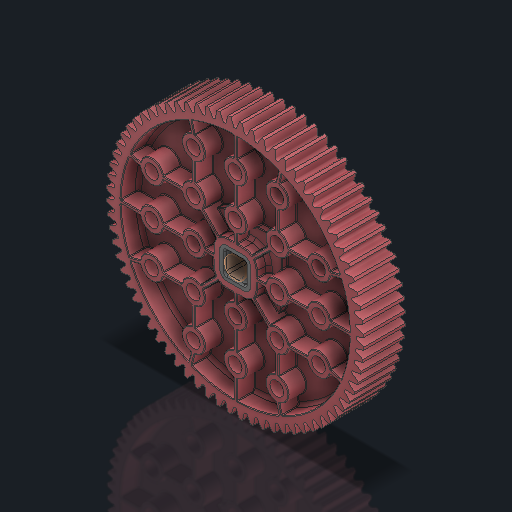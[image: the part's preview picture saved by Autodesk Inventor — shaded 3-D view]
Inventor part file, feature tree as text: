
AUTODESK INVENTOR PART (.ipt)
format: ipt  version: 2023.2 (Build 272271030, 271C)  size: 6,645,248 bytes
history: native  units: in
note: dims shown in document units (in); Inventor stores cm internally (conversion verified against a paired STEP export)
features: other x6, sketch x1
ambient origin geometry x8: Origin, YZ Plane, XZ Plane, XY Plane, X Axis, Y Axis, Z Axis, Center Point
bodies: Solid1 (feature_tree), Solid2 (feature_tree)
feature tree (7):
  other  "HS 72T Gear, No Insert.ipt"
  other  "Solid1::HS 72T Gear, No Insert.ipt"
  other  "Solid2::HS 72T Gear, No Insert.ipt"
  other  "TaggingFeature1"
  sketch  "Sketch1"  dims[d0=0.3937in]
  other  "Srf1"
  other  "Srf1::Derived"
